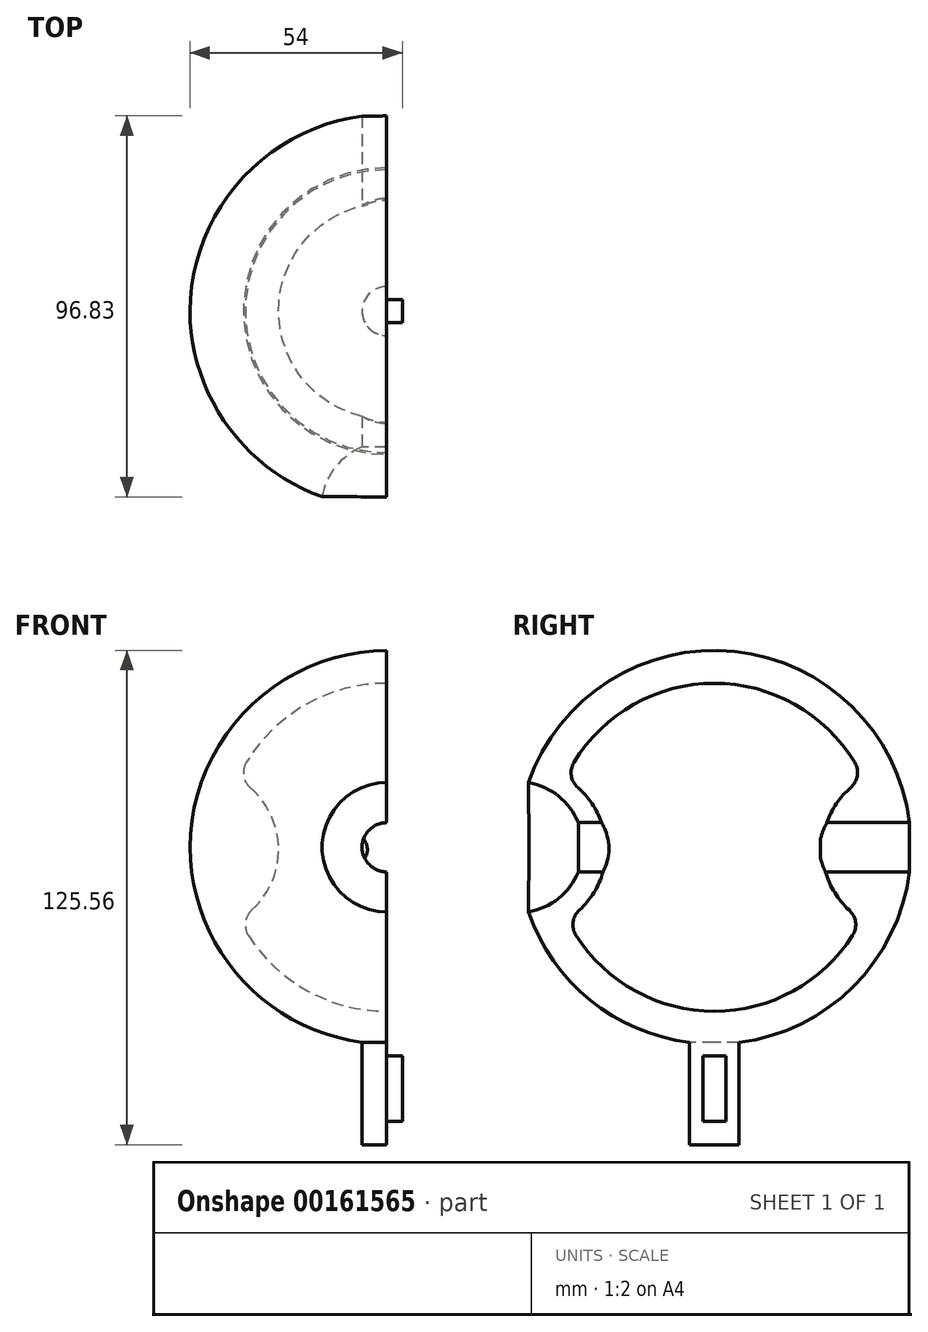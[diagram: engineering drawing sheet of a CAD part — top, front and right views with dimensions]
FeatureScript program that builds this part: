
annotation { "Feature Type Name" : "Feature", "Feature Type Description" : "" }
export const myFeature = defineFeature(function(context is Context, id is Id, definition is map)
    precondition{}
    {
        {
            assignVariable(context, id + "F0", {"name" : "Width", "anyValue" : 100 * mm});
        }
        {
            var Q0;
            Q0=qCreatedBy(makeId("Top.planeOp"),FACE);
            var sketch = newSketch(context, id + "F1", { "sketchPlane" : qUnion([Q0])});
            skArc(sketch, "E0", {"start": v(0, 50) * mm, "mid": v(-35.25, 35.25) * mm, "end": v(-50, 0) * mm});
            skLineSegment(sketch, "E1", {"start": v(-50, 0) * mm, "end": v(0, 0) * mm});
            skLineSegment(sketch, "E2", {"start": v(0, -25.02) * mm, "end": v(0, 61.17) * mm});
            skPoint(sketch, "E3.orphan", {"position": v(50.73, 0) * mm});
            skSolve(sketch);
        }
        {
            var Q0;
            Q0 = qSketchRegion(id + "F1", true);
            var Q1;
            Q1=sQuery(id+"F1.wireOp",EDGE,"E1");
            revolve(context, id + "F2", {"entities" : qUnion([Q0]), "axis" : qUnion([Q1]), "revolveType" : RevolveType.FULL});
        }
        {
            var Q0;
            Q0=qCreatedBy(makeId("Front.planeOp"),FACE);
            cPlane(context, id + "F3", {"entities" : qUnion([Q0]), "cplaneType" : CPlaneType.OFFSET, "offset" : 50 * mm, "width" : 150 * mm, "height" : 150 * mm});
        }
        {
            var Q0;
            Q0=qCreatedBy(id+"F3.planeOp",FACE);
            var sketch = newSketch(context, id + "F4", { "sketchPlane" : qUnion([Q0])});
            skArc(sketch, "E4", {"start": v(0, 16.67) * mm, "mid": v(-16.67, 0) * mm, "end": v(0, -16.67) * mm});
            skLineSegment(sketch, "E5", {"start": v(0, 23.26) * mm, "end": v(0, -27.2) * mm});
            skSolve(sketch);
        }
        {
            var Q0;
            Q0 = qSketchRegion(id + "F4", true);
            var Q1;
            Q1=sQuery(id+"F4.wireOp",EDGE,"E5");
            revolve(context, id + "F5", {"operationType" : NewBodyOperationType.REMOVE, "entities" : qUnion([Q0]), "axis" : qUnion([Q1]), "revolveType" : RevolveType.FULL, "oppositeDirection" : true});
        }
        {
            var Q0;
            Q0=makeQuery(id+"F2.opRevolve","SWEPT_FACE",FACE,{"disambiguationData":[OSD([sQuery(id+"F1.wireOp",EDGE,"E2")])]});
            var sketch = newSketch(context, id + "F6", { "sketchPlane" : qUnion([Q0])});
            skArc(sketch, "E6", {"start": v(-37.42, -18.32) * mm, "mid": v(-22.05, -35.35) * mm, "end": v(0, -41.67) * mm});
            skArc(sketch, "E7", {"start": v(-37.42, -18.32) * mm, "mid": v(-27.48, -0.33) * mm, "end": v(-37.85, 17.43) * mm});
            skLineSegment(sketch, "E8", {"start": v(0, 59.66) * mm, "end": v(0, -56.85) * mm});
            skArc(sketch, "E9.trimOffspring", {"start": v(0, 41.67) * mm, "mid": v(-22.47, 35.09) * mm, "end": v(-37.85, 17.43) * mm});
            skSolve(sketch);
        }
        {
            var Q0;
            Q0 = qSketchRegion(id + "F6", true);
            var Q1;
            Q1=sQuery(id+"F6.wireOp",EDGE,"E8");
            revolve(context, id + "F7", {"operationType" : NewBodyOperationType.REMOVE, "entities" : qUnion([Q0]), "axis" : qUnion([Q1]), "revolveType" : RevolveType.FULL, "oppositeDirection" : true});
        }
        {
            var Q0;
            Q0=makeQuery(id+"F2.opRevolve","SWEPT_FACE",FACE,{"disambiguationData":[OSD([sQuery(id+"F1.wireOp",EDGE,"E2")])]});
            var sketch = newSketch(context, id + "F8", { "sketchPlane" : qUnion([Q0])});
            skLineSegment(sketch, "E10.top", {"start": v(50.36, 6.25) * mm, "end": v(27.03, 6.25) * mm});
            skLineSegment(sketch, "E10.left", {"start": v(50.36, 0) * mm, "end": v(50.36, 6.25) * mm});
            skLineSegment(sketch, "E10.right", {"start": v(27.03, 0) * mm, "end": v(27.03, 6.25) * mm});
            skPoint(sketch, "E10.middle", {"position": v(38.7, 0) * mm});
            skLineSegment(sketch, "E11", {"start": v(50.36, 0) * mm, "end": v(22.73, 0) * mm});
            skPoint(sketch, "E12.orphan", {"position": v(50.36, -6.25) * mm});
            skPoint(sketch, "E13.orphan", {"position": v(27.03, -6.25) * mm});
            skSolve(sketch);
        }
        {
            var Q0;
            Q0 = qSketchRegion(id + "F8", true);
            var Q1;
            Q1=sQuery(id+"F8.wireOp",EDGE,"E11");
            revolve(context, id + "F9", {"operationType" : NewBodyOperationType.REMOVE, "entities" : qUnion([Q0]), "axis" : qUnion([Q1]), "revolveType" : RevolveType.FULL, "oppositeDirection" : true});
        }
        {
            var Q0;
            Q0=makeQuery(id+"F7.boolean.opBoolean","COPY",EDGE,{"derivedFrom":makeQuery(id+"F7.opRevolve","SWEPT_EDGE",EDGE,{"disambiguationData":[OSD([sQuery(id+"F6.wireOp",EDGE,"E7"),sQuery(id+"F6.wireOp",EDGE,"E9.trimOffspring")])]})});
            var Q1;
            Q1=makeQuery(id+"F7.boolean.opBoolean","COPY",EDGE,{"derivedFrom":makeQuery(id+"F7.opRevolve","SWEPT_EDGE",EDGE,{"disambiguationData":[OSD([sQuery(id+"F6.wireOp",EDGE,"E6"),sQuery(id+"F6.wireOp",EDGE,"E7")])]})});
            fillet(context, id + "F10", {"entities" : qUnion([Q0, Q1]), "radius" : 5 * mm, "tangentPropagation" : true, "allowEdgeOverflow" : false});
        }
        {
            var Q0;
            Q0=qCreatedBy(id+"F3.planeOp",FACE);
            var sketch = newSketch(context, id + "F11", { "sketchPlane" : qUnion([Q0])});
            skCircle(sketch, "E14", {"center": v(0, 0) * mm, "radius": 6.25 * mm});
            skSolve(sketch);
        }
        {
            var Q0;
            Q0 = qSketchRegion(id + "F11", true);
            extrude(context, id + "F12", {"entities" : qUnion([Q0]), "operationType" : NewBodyOperationType.REMOVE, "oppositeDirection" : true, "depth" : getVariable(context, 'Width') / 3});
        }
        {
            var Q0;
            Q0=qCreatedBy(makeId("Top.planeOp"),FACE);
            cPlane(context, id + "F13", {"entities" : qUnion([Q0]), "cplaneType" : CPlaneType.OFFSET, "offset" : getVariable(context, 'Width') / 2, "oppositeDirection" : true, "width" : 150 * mm, "height" : 150 * mm});
        }
        {
            var Q0;
            Q0=qCreatedBy(id+"F13.planeOp",FACE);
            var sketch = newSketch(context, id + "F14", { "sketchPlane" : qUnion([Q0])});
            skArc(sketch, "E15", {"start": v(0, 6.25) * mm, "mid": v(-6.25, 0) * mm, "end": v(0, -6.25) * mm});
            skLineSegment(sketch, "E16", {"start": v(0, -6.25) * mm, "end": v(0, 6.25) * mm});
            skPoint(sketch, "E17.orphan", {"position": v(0, -29.48) * mm});
            skSolve(sketch);
        }
        {
            var Q0;
            Q0=makeQuery(id+"F14.imprint","IMPRINT",FACE,{"disambiguationData":[TD([[makeQuery(id+"F14.imprint","IMPRINT",EDGE,{"derivedFrom":sQuery(id+"F14.wireOp",EDGE,"E15")}),1.0]])]});
            extrude(context, id + "F15", {"entities" : qUnion([Q0]), "operationType" : NewBodyOperationType.ADD, "endBound" : BoundingType.SYMMETRIC, "oppositeDirection" : true, "depth" : getVariable(context, 'Width') / 9});
        }
        {
            var Q0;
            Q0=makeQuery(id+"F15.opExtrude","CAP_FACE",FACE,{"disambiguationData":[OSD([sQuery(id+"F14.wireOp",EDGE,"E15"),sQuery(id+"F14.wireOp",EDGE,"E16")])],"isStart":false});
            var sketch = newSketch(context, id + "F16", { "sketchPlane" : qUnion([Q0])});
            skArc(sketch, "E18", {"start": v(0, 6.25) * mm, "mid": v(-6.25, 0) * mm, "end": v(0, -6.25) * mm});
            skLineSegment(sketch, "E19", {"start": v(0, 6.25) * mm, "end": v(0, -6.25) * mm});
            skPoint(sketch, "E20.orphan", {"position": v(0, 13.66) * mm});
            skSolve(sketch);
        }
        {
            var Q0;
            Q0 = qSketchRegion(id + "F16", true);
            extrude(context, id + "F17", {"entities" : qUnion([Q0]), "operationType" : NewBodyOperationType.ADD, "depth" : getVariable(context, 'Width') / 5});
        }
        {
            var Q0;
            {var subQ1=sQuery(id+"F6.wireOp",EDGE,"E6");Q0=makeQuery(id+"F17.boolean.opBoolean","MERGE",FACE,{"derivedFrom":[makeQuery(id+"F15.boolean.opBoolean","MERGE",FACE,{"derivedFrom":[makeQuery(id+"F12.boolean.opBoolean","SPLIT",FACE,{"disambiguationData":[TD([makeQuery(id+"F7.boolean.opBoolean","COPY",FACE,{"derivedFrom":makeQuery(id+"F7.opRevolve","SWEPT_FACE",FACE,{"disambiguationData":[OSD([subQ1])]})})])],"derivedFrom":makeQuery(id+"F2.opRevolve","SWEPT_FACE",FACE,{"disambiguationData":[OSD([sQuery(id+"F1.wireOp",EDGE,"E2")])]})}),makeQuery(id+"F15.opExtrude","SWEPT_FACE",FACE,{"disambiguationData":[OSD([sQuery(id+"F14.wireOp",EDGE,"E16")])]})]}),makeQuery(id+"F17.opExtrude","SWEPT_FACE",FACE,{"disambiguationData":[OSD([sQuery(id+"F16.wireOp",EDGE,"E19")])]})]});}
            var sketch = newSketch(context, id + "F18", { "sketchPlane" : qUnion([Q0])});
            skLineSegment(sketch, "E21.bottom", {"start": v(-2.92, -53.01) * mm, "end": v(-0.59, -53.01) * mm});
            skLineSegment(sketch, "E21.top", {"start": v(-2.92, -69.68) * mm, "end": v(-0.59, -69.68) * mm});
            skLineSegment(sketch, "E21.left", {"start": v(-2.92, -53.01) * mm, "end": v(-2.92, -69.68) * mm});
            skLineSegment(sketch, "E22.MirrorCS", {"start": v(2.92, -53.01) * mm, "end": v(2.92, -69.68) * mm});
            skPoint(sketch, "E23.start.orphan", {"position": v(0, -48.47) * mm});
            skLineSegment(sketch, "E24", {"start": v(-2.92, -53.01) * mm, "end": v(2.92, -53.01) * mm});
            skLineSegment(sketch, "E25", {"start": v(2.92, -69.68) * mm, "end": v(-0.59, -69.68) * mm});
            skSolve(sketch);
        }
        {
            var Q0;
            Q0 = qSketchRegion(id + "F18", true);
            extrude(context, id + "F19", {"entities" : qUnion([Q0]), "operationType" : NewBodyOperationType.ADD, "depth" : getVariable(context, 'Width') / 25});
        }
    });
